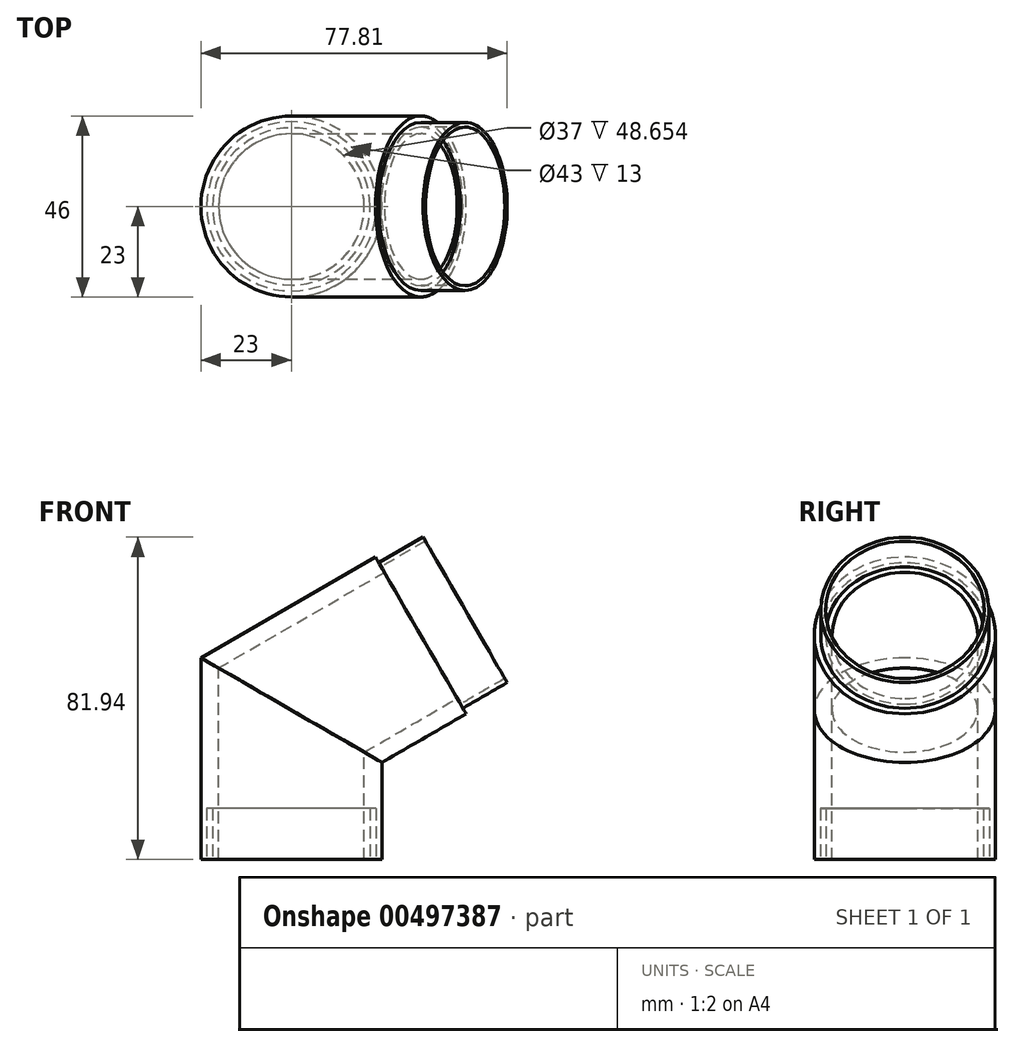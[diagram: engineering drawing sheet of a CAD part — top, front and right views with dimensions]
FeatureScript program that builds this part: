
annotation { "Feature Type Name" : "Feature", "Feature Type Description" : "" }
export const myFeature = defineFeature(function(context is Context, id is Id, definition is map)
    precondition{}
    {
        {
            var Q0;
            Q0=qCreatedBy(makeId("Front.planeOp"),FACE);
            var sketch = newSketch(context, id + "F0", { "sketchPlane" : qUnion([Q0])});
            skLineSegment(sketch, "E0", {"start": v(0, 0) * mm, "end": v(0, 37.97) * mm});
            skLineSegment(sketch, "E1", {"start": v(0, 37.97) * mm, "end": v(32.88, 56.95) * mm});
            skSolve(sketch);
        }
        {
            var Q0;
            Q0=qCreatedBy(makeId("Top.planeOp"),FACE);
            var sketch = newSketch(context, id + "F1", { "sketchPlane" : qUnion([Q0])});
            skPoint(sketch, "E2.0", {"position": v(0, 0) * mm});
            skCircle(sketch, "E3", {"center": v(0, 0) * mm, "radius": 23 * mm});
            skCircle(sketch, "E4.0", {"center": v(0, 0) * mm, "radius": 21.5 * mm});
            skCircle(sketch, "E5.0", {"center": v(0, 0) * mm, "radius": 20 * mm});
            skCircle(sketch, "E6.0", {"center": v(0, 0) * mm, "radius": 18.5 * mm});
            skSolve(sketch);
        }
        {
            var Q0;
            Q0=makeQuery(id+"F1.imprint","IMPRINT",FACE,{"disambiguationData":[TD([[makeQuery(id+"F1.imprint","IMPRINT",EDGE,{"derivedFrom":sQuery(id+"F1.wireOp",EDGE,"E3")}),1.0]])]});
            var Q1;
            Q1=makeQuery(id+"F1.imprint","IMPRINT",FACE,{"disambiguationData":[TD([[makeQuery(id+"F1.imprint","IMPRINT",EDGE,{"derivedFrom":sQuery(id+"F1.wireOp",EDGE,"E5.0")}),1.0]])]});
            var Q2;
            Q2=makeQuery(id+"F1.imprint","IMPRINT",FACE,{"disambiguationData":[TD([[makeQuery(id+"F1.imprint","IMPRINT",EDGE,{"derivedFrom":sQuery(id+"F1.wireOp",EDGE,"E4.0")}),1.0]])]});
            var Q3;
            Q3=sQuery(id+"F0.wireOp",EDGE,"E0");
            var Q4;
            Q4=sQuery(id+"F0.wireOp",EDGE,"E1");
            sweep(context, id + "F2", {"profiles" : qUnion([Q0, Q1, Q2]), "path" : qUnion([Q3, Q4])});
        }
        {
            var Q0;
            Q0=makeQuery(id+"F2.opSweep","CAP_FACE",FACE,{"disambiguationData":[OSD([sQuery(id+"F0.wireOp",VERTEX,"E1.end"),sQuery(id+"F1.wireOp",EDGE,"E3"),sQuery(id+"F1.wireOp",EDGE,"E6.0")])],"isStart":false});
            var sketch = newSketch(context, id + "F3", { "sketchPlane" : qUnion([Q0])});
            skCircle(sketch, "E7.0", {"center": v(0, 32.88) * mm, "radius": 23 * mm});
            skCircle(sketch, "E8.0", {"center": v(0, 32.88) * mm, "radius": 18.5 * mm});
            skCircle(sketch, "E9", {"center": v(0, 32.88) * mm, "radius": 21.35 * mm});
            skCircle(sketch, "E10", {"center": v(0, 32.88) * mm, "radius": 20.15 * mm});
            skSolve(sketch);
        }
        {
            var Q0;
            Q0=makeQuery(id+"F3.imprint","IMPRINT",FACE,{"disambiguationData":[TD([[makeQuery(id+"F3.imprint","IMPRINT",EDGE,{"derivedFrom":sQuery(id+"F3.wireOp",EDGE,"E9")}),1.0]])]});
            extrude(context, id + "F4", {"entities" : qUnion([Q0]), "operationType" : NewBodyOperationType.ADD, "depth" : 13 * mm});
        }
        {
            var Q0;
            Q0=makeQuery(id+"F1.imprint","IMPRINT",FACE,{"disambiguationData":[TD([[makeQuery(id+"F1.imprint","IMPRINT",EDGE,{"derivedFrom":sQuery(id+"F1.wireOp",EDGE,"E4.0")}),1.0]])]});
            extrude(context, id + "F5", {"entities" : qUnion([Q0]), "operationType" : NewBodyOperationType.REMOVE, "depth" : 13 * mm});
        }
    });
